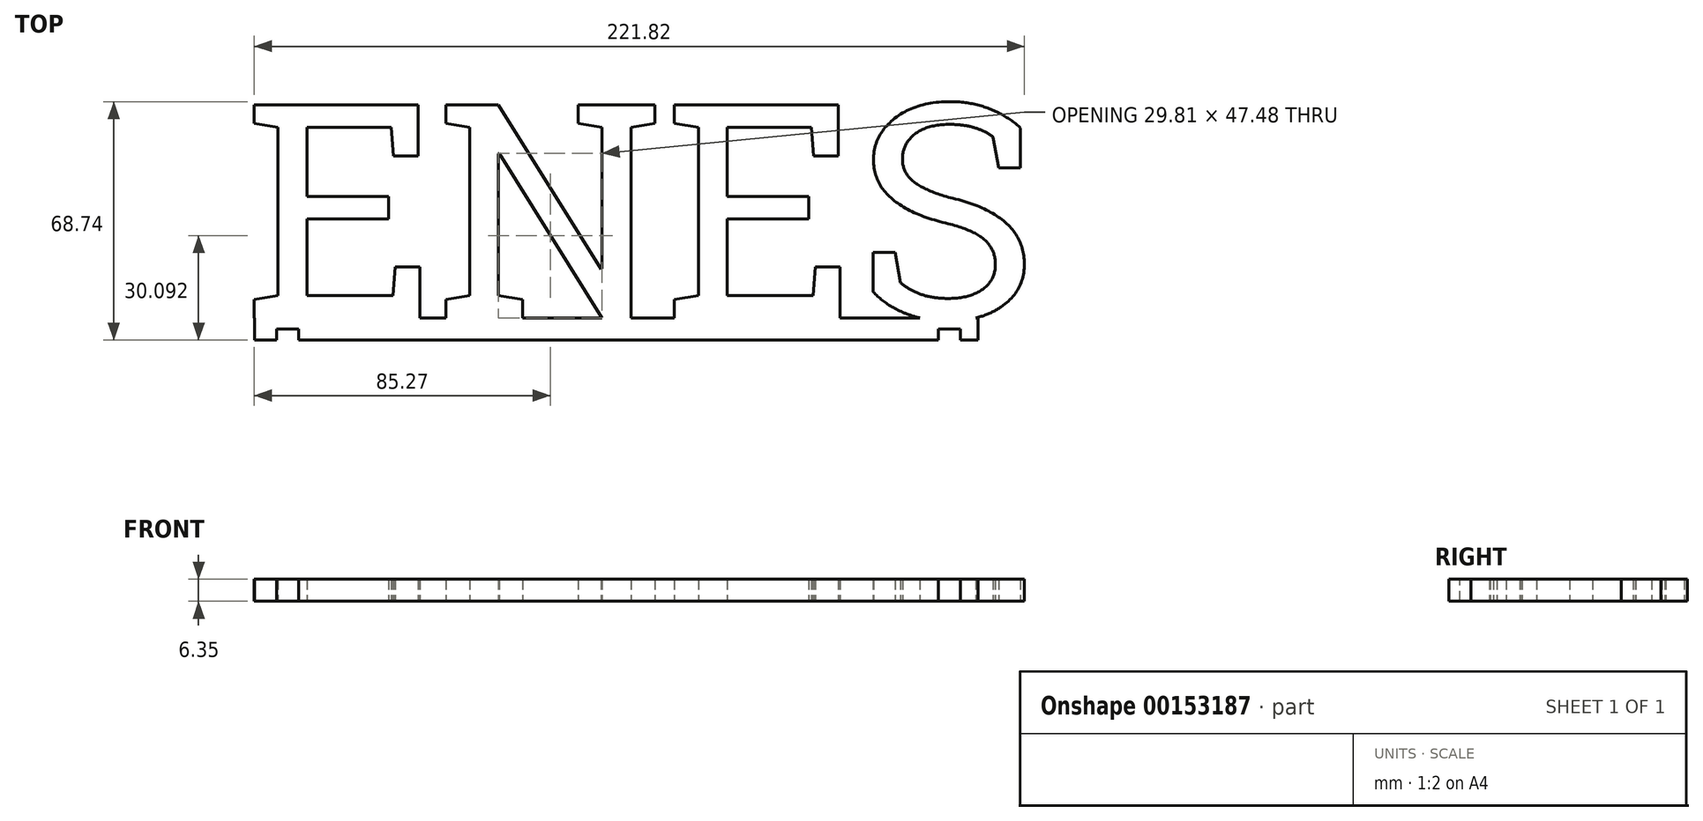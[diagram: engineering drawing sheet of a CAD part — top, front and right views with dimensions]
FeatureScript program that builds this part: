
annotation { "Feature Type Name" : "Feature", "Feature Type Description" : "" }
export const myFeature = defineFeature(function(context is Context, id is Id, definition is map)
    precondition{}
    {
        {
            var Q0;
            Q0=qCreatedBy(makeId("Top.planeOp"),FACE);
            var sketch = newSketch(context, id + "F0", { "sketchPlane" : qUnion([Q0])});
            skText(sketch, "E0", { "text": "ENES", "fontName": "RobotoSlab-Regular.ttf"});
            skLineSegment(sketch, "E1.bottom", {"start": v(187.79, -34.53) * mm, "end": v(-20.64, -34.53) * mm});
            skLineSegment(sketch, "E1.top", {"start": v(187.79, -40.88) * mm, "end": v(-20.64, -40.88) * mm});
            skLineSegment(sketch, "E1.left", {"start": v(187.79, -34.53) * mm, "end": v(187.79, -40.88) * mm});
            skLineSegment(sketch, "E1.right", {"start": v(-20.64, -34.53) * mm, "end": v(-20.64, -40.88) * mm});
            const initialGuessF0  = {"E0": [-0.0237, -0.03453, 1, 0, 0.06228]};
            skSetInitialGuess(sketch, initialGuessF0);
            skSolve(sketch);
        }
        {
            var Q0;
            Q0 = qSketchRegion(id + "F0", true);
            extrude(context, id + "F1", {"entities" : qUnion([Q0]), "depth" : 6.35 * mm});
        }
        {
            var Q0;
            Q0=makeQuery(id+"F1.opExtrude","CAP_FACE",FACE,{"disambiguationData":[OSD([sQuery(id+"F0.wireOp",EDGE,"E0.sketch_text.stroke-0"),sQuery(id+"F0.wireOp",EDGE,"E0.sketch_text.stroke-1"),sQuery(id+"F0.wireOp",EDGE,"E0.sketch_text.stroke-2"),sQuery(id+"F0.wireOp",EDGE,"E0.sketch_text.stroke-3"),sQuery(id+"F0.wireOp",EDGE,"E0.sketch_text.stroke-4"),sQuery(id+"F0.wireOp",EDGE,"E0.sketch_text.stroke-5"),sQuery(id+"F0.wireOp",EDGE,"E0.sketch_text.stroke-6"),sQuery(id+"F0.wireOp",EDGE,"E0.sketch_text.stroke-7"),sQuery(id+"F0.wireOp",EDGE,"E0.sketch_text.stroke-8"),sQuery(id+"F0.wireOp",EDGE,"E0.sketch_text.stroke-9"),sQuery(id+"F0.wireOp",EDGE,"E0.sketch_text.stroke-10"),sQuery(id+"F0.wireOp",EDGE,"E0.sketch_text.stroke-11"),sQuery(id+"F0.wireOp",EDGE,"E0.sketch_text.stroke-12"),sQuery(id+"F0.wireOp",EDGE,"E0.sketch_text.stroke-13"),sQuery(id+"F0.wireOp",EDGE,"E0.sketch_text.stroke-14"),sQuery(id+"F0.wireOp",EDGE,"E0.sketch_text.stroke-15"),sQuery(id+"F0.wireOp",EDGE,"E0.sketch_text.stroke-16"),sQuery(id+"F0.wireOp",EDGE,"E0.sketch_text.stroke-17"),sQuery(id+"F0.wireOp",EDGE,"E0.sketch_text.stroke-18"),sQuery(id+"F0.wireOp",EDGE,"E0.sketch_text.stroke-19"),sQuery(id+"F0.wireOp",EDGE,"E0.sketch_text.stroke-20"),sQuery(id+"F0.wireOp",EDGE,"E0.sketch_text.stroke-21"),sQuery(id+"F0.wireOp",EDGE,"E0.sketch_text.stroke-22"),sQuery(id+"F0.wireOp",EDGE,"E0.sketch_text.stroke-24"),sQuery(id+"F0.wireOp",EDGE,"E0.sketch_text.stroke-25"),sQuery(id+"F0.wireOp",EDGE,"E0.sketch_text.stroke-26"),sQuery(id+"F0.wireOp",EDGE,"E0.sketch_text.stroke-27"),sQuery(id+"F0.wireOp",EDGE,"E0.sketch_text.stroke-28"),sQuery(id+"F0.wireOp",EDGE,"E0.sketch_text.stroke-30"),sQuery(id+"F0.wireOp",EDGE,"E0.sketch_text.stroke-31"),sQuery(id+"F0.wireOp",EDGE,"E0.sketch_text.stroke-32"),sQuery(id+"F0.wireOp",EDGE,"E0.sketch_text.stroke-33"),sQuery(id+"F0.wireOp",EDGE,"E0.sketch_text.stroke-34"),sQuery(id+"F0.wireOp",EDGE,"E0.sketch_text.stroke-35"),sQuery(id+"F0.wireOp",EDGE,"E0.sketch_text.stroke-36"),sQuery(id+"F0.wireOp",EDGE,"E0.sketch_text.stroke-37"),sQuery(id+"F0.wireOp",EDGE,"E0.sketch_text.stroke-38"),sQuery(id+"F0.wireOp",EDGE,"E0.sketch_text.stroke-39"),sQuery(id+"F0.wireOp",EDGE,"E0.sketch_text.stroke-40"),sQuery(id+"F0.wireOp",EDGE,"E0.sketch_text.stroke-41"),sQuery(id+"F0.wireOp",EDGE,"E0.sketch_text.stroke-42"),sQuery(id+"F0.wireOp",EDGE,"E0.sketch_text.stroke-43"),sQuery(id+"F0.wireOp",EDGE,"E0.sketch_text.stroke-44"),sQuery(id+"F0.wireOp",EDGE,"E0.sketch_text.stroke-45"),sQuery(id+"F0.wireOp",EDGE,"E0.sketch_text.stroke-46"),sQuery(id+"F0.wireOp",EDGE,"E0.sketch_text.stroke-47"),sQuery(id+"F0.wireOp",EDGE,"E0.sketch_text.stroke-48"),sQuery(id+"F0.wireOp",EDGE,"E0.sketch_text.stroke-49"),sQuery(id+"F0.wireOp",EDGE,"E0.sketch_text.stroke-50"),sQuery(id+"F0.wireOp",EDGE,"E0.sketch_text.stroke-51"),sQuery(id+"F0.wireOp",EDGE,"E0.sketch_text.stroke-52"),sQuery(id+"F0.wireOp",EDGE,"E0.sketch_text.stroke-53"),sQuery(id+"F0.wireOp",EDGE,"E0.sketch_text.stroke-54"),sQuery(id+"F0.wireOp",EDGE,"E0.sketch_text.stroke-55"),sQuery(id+"F0.wireOp",EDGE,"E0.sketch_text.stroke-56"),sQuery(id+"F0.wireOp",EDGE,"E0.sketch_text.stroke-57"),sQuery(id+"F0.wireOp",EDGE,"E0.sketch_text.stroke-58"),sQuery(id+"F0.wireOp",EDGE,"E0.sketch_text.stroke-59"),sQuery(id+"F0.wireOp",EDGE,"E0.sketch_text.stroke-60"),sQuery(id+"F0.wireOp",EDGE,"E0.sketch_text.stroke-61"),sQuery(id+"F0.wireOp",EDGE,"E0.sketch_text.stroke-62"),sQuery(id+"F0.wireOp",EDGE,"E0.sketch_text.stroke-64"),sQuery(id+"F0.wireOp",EDGE,"E0.sketch_text.stroke-65"),sQuery(id+"F0.wireOp",EDGE,"E0.sketch_text.stroke-66"),sQuery(id+"F0.wireOp",EDGE,"E0.sketch_text.stroke-67"),sQuery(id+"F0.wireOp",EDGE,"E0.sketch_text.stroke-68"),sQuery(id+"F0.wireOp",EDGE,"E0.sketch_text.stroke-69"),sQuery(id+"F0.wireOp",EDGE,"E0.sketch_text.stroke-70"),sQuery(id+"F0.wireOp",EDGE,"E0.sketch_text.stroke-71"),sQuery(id+"F0.wireOp",EDGE,"E0.sketch_text.stroke-72"),sQuery(id+"F0.wireOp",EDGE,"E0.sketch_text.stroke-73"),sQuery(id+"F0.wireOp",EDGE,"E0.sketch_text.stroke-74"),sQuery(id+"F0.wireOp",EDGE,"E0.sketch_text.stroke-75"),sQuery(id+"F0.wireOp",EDGE,"E0.sketch_text.stroke-76"),sQuery(id+"F0.wireOp",EDGE,"E0.sketch_text.stroke-77"),sQuery(id+"F0.wireOp",EDGE,"E0.sketch_text.stroke-78"),sQuery(id+"F0.wireOp",EDGE,"E0.sketch_text.stroke-79"),sQuery(id+"F0.wireOp",EDGE,"E0.sketch_text.stroke-80"),sQuery(id+"F0.wireOp",EDGE,"E0.sketch_text.stroke-81"),sQuery(id+"F0.wireOp",EDGE,"E0.sketch_text.stroke-82"),sQuery(id+"F0.wireOp",EDGE,"E0.sketch_text.stroke-83"),sQuery(id+"F0.wireOp",EDGE,"E0.sketch_text.stroke-84"),sQuery(id+"F0.wireOp",EDGE,"E0.sketch_text.stroke-85"),sQuery(id+"F0.wireOp",EDGE,"E0.sketch_text.stroke-86"),sQuery(id+"F0.wireOp",EDGE,"E0.sketch_text.stroke-87"),sQuery(id+"F0.wireOp",EDGE,"E0.sketch_text.stroke-88"),sQuery(id+"F0.wireOp",EDGE,"E0.sketch_text.stroke-89"),sQuery(id+"F0.wireOp",EDGE,"E0.sketch_text.stroke-90"),sQuery(id+"F0.wireOp",EDGE,"E0.sketch_text.stroke-91"),sQuery(id+"F0.wireOp",EDGE,"E0.sketch_text.stroke-92"),sQuery(id+"F0.wireOp",EDGE,"E0.sketch_text.stroke-93"),sQuery(id+"F0.wireOp",EDGE,"E1.bottom"),sQuery(id+"F0.wireOp",EDGE,"E1.top"),sQuery(id+"F0.wireOp",EDGE,"E1.left"),sQuery(id+"F0.wireOp",EDGE,"E1.right")])],"isStart":false});
            var sketch = newSketch(context, id + "F2", { "sketchPlane" : qUnion([Q0])});
            skLineSegment(sketch, "E2.bottom", {"start": v(-14.3, -40.88) * mm, "end": v(-7.94, -40.88) * mm});
            skLineSegment(sketch, "E2.top", {"start": v(-14.3, -37.7) * mm, "end": v(-7.94, -37.7) * mm});
            skLineSegment(sketch, "E2.left", {"start": v(-14.3, -40.88) * mm, "end": v(-14.3, -37.7) * mm});
            skLineSegment(sketch, "E2.right", {"start": v(-7.94, -40.88) * mm, "end": v(-7.94, -37.7) * mm});
            skLineSegment(sketch, "E3.bottom", {"start": v(176.36, -40.88) * mm, "end": v(182.7, -40.88) * mm});
            skLineSegment(sketch, "E3.top", {"start": v(176.36, -37.7) * mm, "end": v(182.7, -37.7) * mm});
            skLineSegment(sketch, "E3.left", {"start": v(176.36, -40.88) * mm, "end": v(176.36, -37.7) * mm});
            skLineSegment(sketch, "E3.right", {"start": v(182.7, -40.88) * mm, "end": v(182.7, -37.7) * mm});
            skSolve(sketch);
        }
        {
            var Q0;
            Q0=makeQuery(id+"F2.imprint","IMPRINT",FACE,{"disambiguationData":[TD([[makeQuery(id+"F2.imprint","IMPRINT",EDGE,{"derivedFrom":sQuery(id+"F2.wireOp",EDGE,"E2.bottom")}),-1.0]])]});
            var Q1;
            Q1=makeQuery(id+"F2.imprint","IMPRINT",FACE,{"disambiguationData":[TD([[makeQuery(id+"F2.imprint","IMPRINT",EDGE,{"derivedFrom":sQuery(id+"F2.wireOp",EDGE,"E3.bottom")}),-1.0]])]});
            extrude(context, id + "F3", {"entities" : qUnion([Q0, Q1]), "operationType" : NewBodyOperationType.REMOVE, "oppositeDirection" : true, "depth" : 25.4 * mm});
        }
    });
